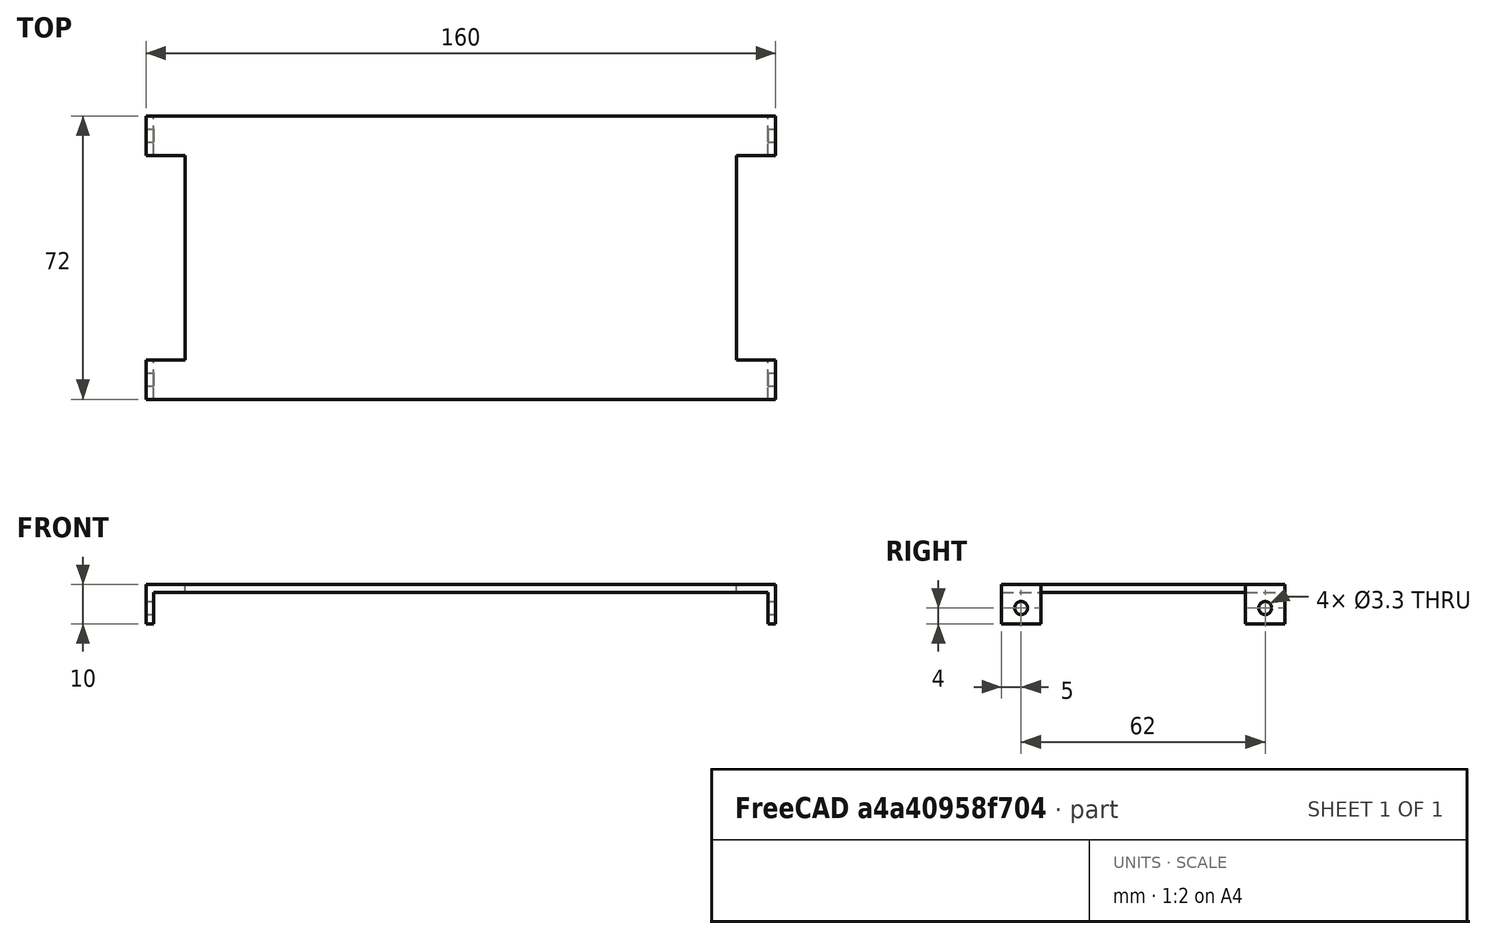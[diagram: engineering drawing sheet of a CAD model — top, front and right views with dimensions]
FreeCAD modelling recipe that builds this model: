
FCSTD DOCUMENT  (FreeCAD 0.17R13522 (Git))
Label: Zwischenblech
License: All rights reserved
LicenseURL: http://en.wikipedia.org/wiki/All_rights_reserved
objects: TechDraw::DrawViewDimension×12, Part::Box×3, Part::Cut×3, TechDraw::DrawProjGroupItem×3, Part::Mirroring×1, PartDesign::FeatureBase×1, Sketcher::SketchObject×1, PartDesign::Hole×1, PartDesign::Body×1, TechDraw::DrawSVGTemplate×1, TechDraw::DrawProjGroup×1, TechDraw::DrawPage×1
note: 12 computed .brp shape members not serialized (recipe doc carries the construction recipe); baked Part::Feature solids carry a one-line shape summary decoded from their .brp

FEATURE [Part::Box] Box  label="Würfel"
  AttacherType = Attacher::AttachEngine3D
  Height = 10
  Length = 160
  Width = 72
FEATURE [Part::Box] Box001  label="Würfel001"
  AttacherType = Attacher::AttachEngine3D
  Height = 10
  Length = 10
  Placement = pos=(0,10,0) rot=(0,0,1;0rad)
  Width = 52
FEATURE [Part::Mirroring] Part__Mirroring  label="Würfel001 (Mirror #1)"
  Base = (80,0,0)
  Normal = (1,0,0)
  Source = -> Box001
FEATURE [Part::Cut] Cut
  Base = -> Box
  Tool = -> Box001
FEATURE [Part::Cut] Cut001
  Base = -> Cut
  Tool = -> Part__Mirroring
FEATURE [Part::Box] Box002  label="Würfel002"
  AttacherType = Attacher::AttachEngine3D
  Height = 8
  Length = 156
  Placement = pos=(2,0,0) rot=(0,0,1;0rad)
  Width = 72
FEATURE [Part::Cut] Cut002
  Base = -> Cut001
  Tool = -> Box002
FEATURE [PartDesign::FeatureBase] BaseFeature
  BaseFeature = -> Cut002
FEATURE [Sketcher::SketchObject] Sketch
  MapMode = 5
  Placement = pos=(0,0,0) rot=(0.57735,-0.57735,-0.57735;2.0944rad)
  Support = -> [BaseFeature]
  sketch-geometry (2):
    g0: Circle CenterX=-5 CenterY=4 CenterZ=0 NormalX=0 NormalY=0 NormalZ=1 AngleXU=0 Radius=2.2
    g1: Circle CenterX=-67 CenterY=4 CenterZ=0 NormalX=0 NormalY=0 NormalZ=1 AngleXU=0 Radius=2.2
  constraints (6):
    c: Horizontal(g0,g1)
    c: DistanceY(g-1,g0) = 4
    c: Radius(g0) = 2.2
    c: Radius(g1) = 2.2
    c: DistanceX(g0,g-1) = 5
    c: DistanceX(g1,g-1) = 67
FEATURE [PartDesign::Hole] Hole
  BaseFeature = -> BaseFeature
  Depth = 25
  DepthType = 1
  Diameter = 3.3
  DrillPoint = 1
  DrillPointAngle = 118
  HoleCutCountersinkAngle = 90
  HoleCutDepth = 0
  HoleCutDiameter = 3
  HoleCutType = 0
  ModelActualThread = false
  Profile = -> Sketch
  Tapered = false
  TaperedAngle = 90
  ThreadAngle = 0
  ThreadClass = 0
  ThreadCutOffInner = 0
  ThreadCutOffOuter = 0
  ThreadDirection = 0
  ThreadFit = 0
  ThreadPitch = 0
  ThreadSize = 3
  ThreadType = 1
  Threaded = false
FEATURE [PartDesign::Body] Body
  BaseFeature = -> Cut002
  Group = -> [BaseFeature,Sketch,Hole]
  Origin = -> Origin
  Tip = -> Hole
FEATURE [TechDraw::DrawSVGTemplate] Template
  EditableTexts = Designed_by_Name=Christian Dengler; FC-Date=25.04.2018; FC-SC=Scale; FC-SH=1/1; FC-Title=Zwischenblech
  Height = 210
  Orientation = 1
  Width = 297
FEATURE [TechDraw::DrawProjGroupItem] ProjItem  label="Front"
  CoarseView = false
  Direction = (0,-1,0)
  Focus = 100
  HardHidden = false
  IsoCount = 0
  IsoHidden = false
  IsoVisible = false
  LockPosition = false
  Perspective = false
  Rotation = 0
  RotationVector = (1,0,0)
  ScaleType = 0
  SeamHidden = false
  SeamVisible = false
  SmoothHidden = false
  SmoothVisible = false
  Source = -> [Body]
  Type = 0
  X = 0
  Y = 63.9337
FEATURE [TechDraw::DrawProjGroupItem] ProjItem001  label="Top"
  CoarseView = false
  Direction = (0,0,1)
  Focus = 100
  HardHidden = false
  IsoCount = 0
  IsoHidden = false
  IsoVisible = false
  LockPosition = false
  Perspective = false
  Rotation = 0
  RotationVector = (1,0,0)
  ScaleType = 0
  SeamHidden = false
  SeamVisible = false
  SmoothHidden = false
  SmoothVisible = false
  Source = -> [Body]
  Type = 4
  X = 0
  Y = -72.6
FEATURE [TechDraw::DrawProjGroupItem] ProjItem002  label="Left"
  CoarseView = false
  Direction = (-1,0,0)
  Focus = 100
  HardHidden = false
  IsoCount = 0
  IsoHidden = false
  IsoVisible = false
  LockPosition = true
  Perspective = false
  Rotation = 0
  RotationVector = (0,1,0)
  ScaleType = 0
  SeamHidden = false
  SeamVisible = false
  SmoothHidden = false
  SmoothVisible = false
  Source = -> [Body]
  Type = 1
  X = 132.721
  Y = 0
FEATURE [TechDraw::DrawProjGroup] ProjGroup
  Anchor = -> ProjItem
  AutoDistribute = true
  CubeDirs = (6) [(1.22465e-16,-2.44929e-16,-1),(1.93086e-32,-1,2.44929e-16),(-1,-2.46519e-32,-1.22465e-16),(-1.93086e-32,1,-2.44929e-16),(1,2.46519e-32,1.22465e-16),(-1.22465e-16,2.44929e-16,1)]
  CubeRotations = (6) [(1,2.46519e-32,1.22465e-16),(1,2.46519e-32,1.22465e-16),(4.89859e-16,1,-3.67394e-16),(-1,-2.46519e-32,-1.22465e-16),(-4.89859e-16,-1,3.67394e-16),(1,2.46519e-32,1.22465e-16)]
  LockPosition = false
  ProjectionType = 0
  Rotation = 0
  Scale = 0.8
  ScaleType = 2
  Source = -> [Body]
  Views = -> [ProjItem,ProjItem001,ProjItem002]
  X = 86.5544
  Y = 185.3
  spacingX = 15
  spacingY = 15
FEATURE [TechDraw::DrawViewDimension] Dimension
  FormatSpec = %.2f
  LockPosition = false
  MeasureType = 1
  References2D = -> [ProjItem002]
  Rotation = 0
  ScaleType = 0
  Type = 1
  X = 10.2351
  Y = -17.5972
FEATURE [TechDraw::DrawViewDimension] Dimension001
  FormatSpec = %.2f
  LockPosition = false
  MeasureType = 1
  References2D = -> [ProjItem002]
  Rotation = 0
  ScaleType = 0
  Type = 1
  X = 0.987597
  Y = -25.0491
FEATURE [TechDraw::DrawViewDimension] Dimension002
  FormatSpec = %.2f
  LockPosition = false
  MeasureType = 1
  References2D = -> [ProjItem002]
  Rotation = 0
  ScaleType = 0
  Type = 2
  X = 47.8334
  Y = -23.0061
FEATURE [TechDraw::DrawViewDimension] Dimension003
  FormatSpec = %.2f
  LockPosition = false
  MeasureType = 1
  References2D = -> [ProjItem002]
  Rotation = 0
  ScaleType = 0
  Type = 2
  X = 56.1444
  Y = -22.5771
FEATURE [TechDraw::DrawViewDimension] Dimension004
  FormatSpec = %.2f
  LockPosition = false
  MeasureType = 1
  References2D = -> [ProjItem001]
  Rotation = 0
  ScaleType = 0
  Type = 2
  X = 71.7869
  Y = -7.74972
FEATURE [TechDraw::DrawViewDimension] Dimension005
  FormatSpec = %.2f
  LockPosition = false
  MeasureType = 1
  References2D = -> [ProjItem001]
  Rotation = 0
  ScaleType = 0
  Type = 2
  X = 82.1879
  Y = -8.36155
FEATURE [TechDraw::DrawViewDimension] Dimension006
  FormatSpec = %.2f
  LockPosition = false
  MeasureType = 1
  References2D = -> [ProjItem001]
  Rotation = 0
  ScaleType = 0
  Type = 2
  X = 93.2006
  Y = -7.54579
FEATURE [TechDraw::DrawViewDimension] Dimension007
  FormatSpec = %.2f
  LockPosition = false
  MeasureType = 1
  References2D = -> [ProjItem001]
  Rotation = 0
  ScaleType = 0
  Type = 1
  X = 37.5902
  Y = 36.7092
FEATURE [TechDraw::DrawViewDimension] Dimension008
  FormatSpec = %.2f
  LockPosition = false
  MeasureType = 1
  References2D = -> [ProjItem001]
  Rotation = 0
  ScaleType = 0
  Type = 1
  X = 37.2966
  Y = 44.0511
FEATURE [TechDraw::DrawViewDimension] Dimension009
  FormatSpec = %.2f
  LockPosition = false
  MeasureType = 1
  References2D = -> [ProjItem001]
  Rotation = 0
  ScaleType = 0
  Type = 1
  X = 8.81021
  Y = 53.4486
FEATURE [TechDraw::DrawViewDimension] Dimension010
  FormatSpec = %.2f
  LockPosition = false
  MeasureType = 1
  References2D = -> [ProjItem]
  Rotation = 0
  ScaleType = 0
  Type = 1
  X = 50.0335
  Y = -8.66212
FEATURE [TechDraw::DrawViewDimension] Dimension011
  FormatSpec = %.2f
  LockPosition = false
  MeasureType = 1
  References2D = -> [ProjItem002]
  Rotation = 0
  ScaleType = 0
  Type = 5
  X = -52.7117
  Y = 9.58519
FEATURE [TechDraw::DrawPage] Page
  KeepUpdated = true
  ProjectionType = 0
  Template = -> Template
  Views = -> [ProjGroup,Dimension,Dimension001,Dimension002,Dimension003,Dimension004,Dimension005,Dimension006,Dimension007,Dimension008,Dimension009,Dimension010,Dimension011]
